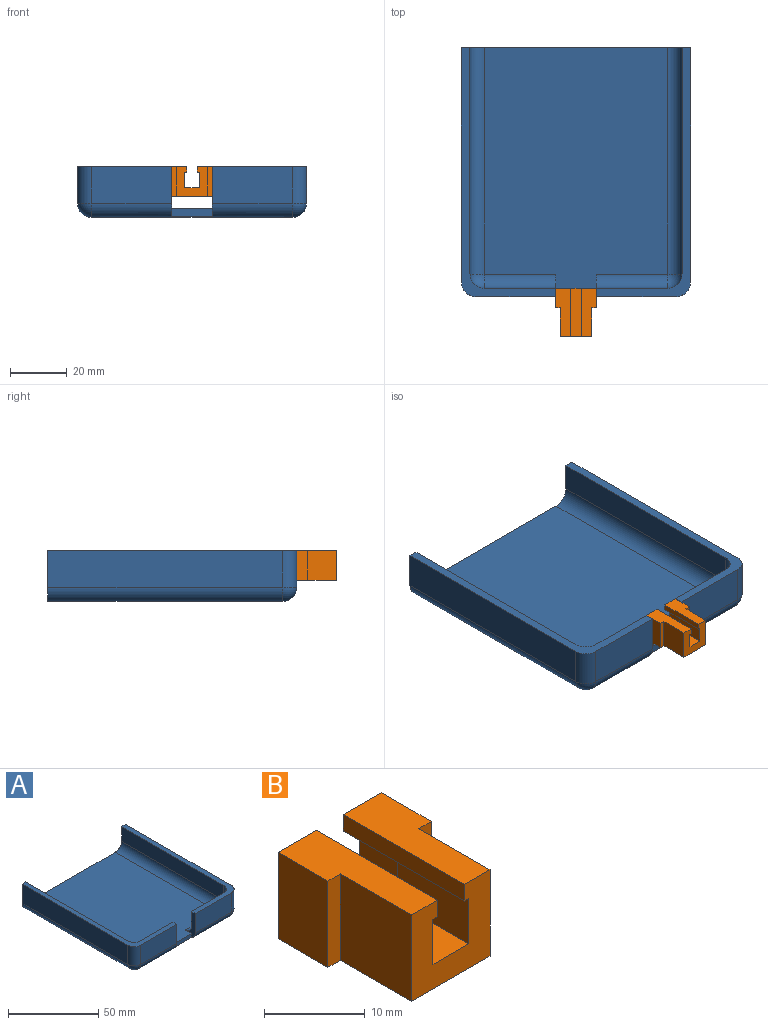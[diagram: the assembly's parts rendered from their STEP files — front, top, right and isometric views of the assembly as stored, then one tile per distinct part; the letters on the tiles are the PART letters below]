
ASSEMBLY  parts=2 mates=1
PART A: 31 faces, bbox 81x88x18 mm
  f0: plane 14.5x2.58mm, normal (0,-1,0), area 37.4mm2, adj f2,f8,f12,f27
  f1: plane 81x18mm, normal (0,1,0), area 333mm2, adj f2,f3,f4,f6,f9,f11,f14,f15
  f2: plane 85x65mm, normal (0,0,1), area 5272.5mm2, adj f0,f1,f8,f12,f17,f19,f21,f23
  f3: plane 83x71mm, normal (0,0,-1), area 5893mm2, adj f1,f24,f27,f28
  f4: plane 80x10mm, normal (1,0,0), area 800mm2, adj f1,f9,f16,f17
  f5: plane 25.25x10mm, normal (0,1,0), area 252.5mm2, adj f8,f9,f16,f19
  f6: plane 83x13mm, normal (-1,0,0), area 1079mm2, adj f1,f9,f24,f25
  f7: plane 28.25x13mm, normal (0,-1,0), area 367.2mm2, adj f8,f9,f25,f27
  f8: plane 17.58x8mm, normal (1,0,0), area 54.3mm2, adj f0,f2,f5,f7,f9,f19,f27
  f9: plane 88x33.25mm, normal (0,0,1), area 354.8mm2, adj f1,f4,f5,f6,f7,f8,f16,f25
  f10: plane 25.25x10mm, normal (0,1,0), area 252.5mm2, adj f12,f15,f20,f21
  f11: plane 80x10mm, normal (-1,0,0), area 800mm2, adj f1,f15,f20,f23
  f12: plane 17.58x8mm, normal (-1,0,0), area 54.3mm2, adj f0,f2,f10,f13,f15,f21,f27
  f13: plane 28.25x13mm, normal (0,-1,0), area 367.2mm2, adj f12,f15,f27,f30
  f14: plane 83x13mm, normal (1,0,0), area 1079mm2, adj f1,f15,f28,f30
  f15: plane 88x33.25mm, normal (0,0,1), area 354.7mm2, adj f1,f10,f11,f12,f13,f14,f20,f30
  f16: cylinder r=5mm len=10mm, axis (0,0,-1), area 78.5mm2, adj f4,f5,f9,f18
  f17: cylinder r=5mm len=80mm, axis (0,1,0), area 628.3mm2, adj f1,f2,f4,f18
  f18: sphere r=5mm, area 39.3mm2, adj f16,f17,f19
  f19: cylinder r=5mm len=25.25mm, axis (-1,0,0), area 198.3mm2, adj f2,f5,f8,f18
  f20: cylinder r=5mm len=10mm, axis (0,0,1), area 78.5mm2, adj f10,f11,f15,f22
  f21: cylinder r=5mm len=25.25mm, axis (-1,0,0), area 198.3mm2, adj f2,f10,f12,f22
  f22: sphere r=5mm, area 39.3mm2, adj f20,f21,f23
  f23: cylinder r=5mm len=80mm, axis (0,-1,0), area 628.3mm2, adj f1,f2,f11,f22
  f24: cylinder r=5mm len=83mm, axis (0,-1,0), area 651.9mm2, adj f1,f3,f6,f26
  f25: cylinder r=5mm len=13mm, axis (0,0,-1), area 102.1mm2, adj f6,f7,f9,f26
  f26: sphere r=5mm, area 39.3mm2, adj f24,f25,f27
  f27: cylinder r=5mm len=71mm, axis (1,0,0), area 473.6mm2, adj f0,f3,f7,f8,f12,f13,f26,f29
  f28: cylinder r=5mm len=83mm, axis (0,1,0), area 651.9mm2, adj f1,f3,f14,f29
  f29: sphere r=5mm, area 39.3mm2, adj f27,f28,f30
  f30: cylinder r=5mm len=13mm, axis (0,0,1), area 102.1mm2, adj f13,f14,f15,f29
PART B: 22 faces, bbox 14.5x17x10.5 mm
  f0: plane 17x8.5mm, normal (0,0,1), area 109.5mm2, adj f1,f5,f10,f11,f12,f13,f14,f15
  f1: plane 14.5x10.5mm, normal (0,1,0), area 97.9mm2, adj f0,f2,f8,f9,f11,f13,f16,f17
  f2: plane 10.5x7mm, normal (-1,0,0), area 73.5mm2, adj f1,f3,f9,f17
  f3: plane 10.5x1.75mm, normal (0,-1,0), area 18.4mm2, adj f2,f4,f9,f17
  f4: plane 10.5x10mm, normal (-1,0,0), area 105mm2, adj f3,f5,f9,f17
  f5: plane 11x10.5mm, normal (0,-1,0), area 80.4mm2, adj f0,f4,f6,f9,f12,f15,f16,f17
  f6: plane 10.5x10mm, normal (1,0,0), area 105mm2, adj f5,f7,f9,f21
  f7: plane 10.5x1.75mm, normal (0,-1,0), area 18.4mm2, adj f6,f8,f9,f21
  f8: plane 10.5x7mm, normal (1,0,0), area 73.5mm2, adj f1,f7,f9,f21
  f9: plane 17x14.5mm, normal (0,0,-1), area 211.5mm2, adj f1,f2,f3,f4,f5,f6,f7,f8
  f10: plane 5.5x1.75mm, normal (0,1,0), area 9.6mm2, adj f0,f11,f12,f18
  f11: plane 7x5.5mm, normal (1,0,0), area 38.5mm2, adj f0,f1,f10,f18
  f12: plane 10x5.5mm, normal (1,0,0), area 55mm2, adj f0,f5,f10,f18
  f13: plane 7x5.5mm, normal (-1,0,0), area 38.5mm2, adj f0,f1,f14,f19
  f14: plane 5.5x1.75mm, normal (0,1,0), area 9.6mm2, adj f0,f13,f15,f19
  f15: plane 10x5.5mm, normal (-1,0,0), area 55mm2, adj f0,f5,f14,f19
  f16: plane 17x2mm, normal (1,0,0), area 34mm2, adj f1,f5,f17,f18
  f17: plane 17x5.35mm, normal (0,0,1), area 73.5mm2, adj f1,f2,f3,f4,f5,f16
  f18: plane 17x2.35mm, normal (0,0,-1), area 22.5mm2, adj f1,f5,f10,f11,f12,f16
  f19: plane 17x2.35mm, normal (0,0,-1), area 22.4mm2, adj f1,f5,f13,f14,f15,f20
  f20: plane 17x2mm, normal (-1,0,0), area 34mm2, adj f1,f5,f19,f21
  f21: plane 17x5.35mm, normal (0,0,1), area 73.4mm2, adj f1,f5,f6,f7,f8,f20
PLACE A t=(-5.95,-6.4,-13.45)mm
PLACE B t=(-1.7,-55.9,-2.95)mm
MATE fastened B.f2 <-> A.f8  axis (-1,0,0) through (-13.2,-48.9,4.55)mm
